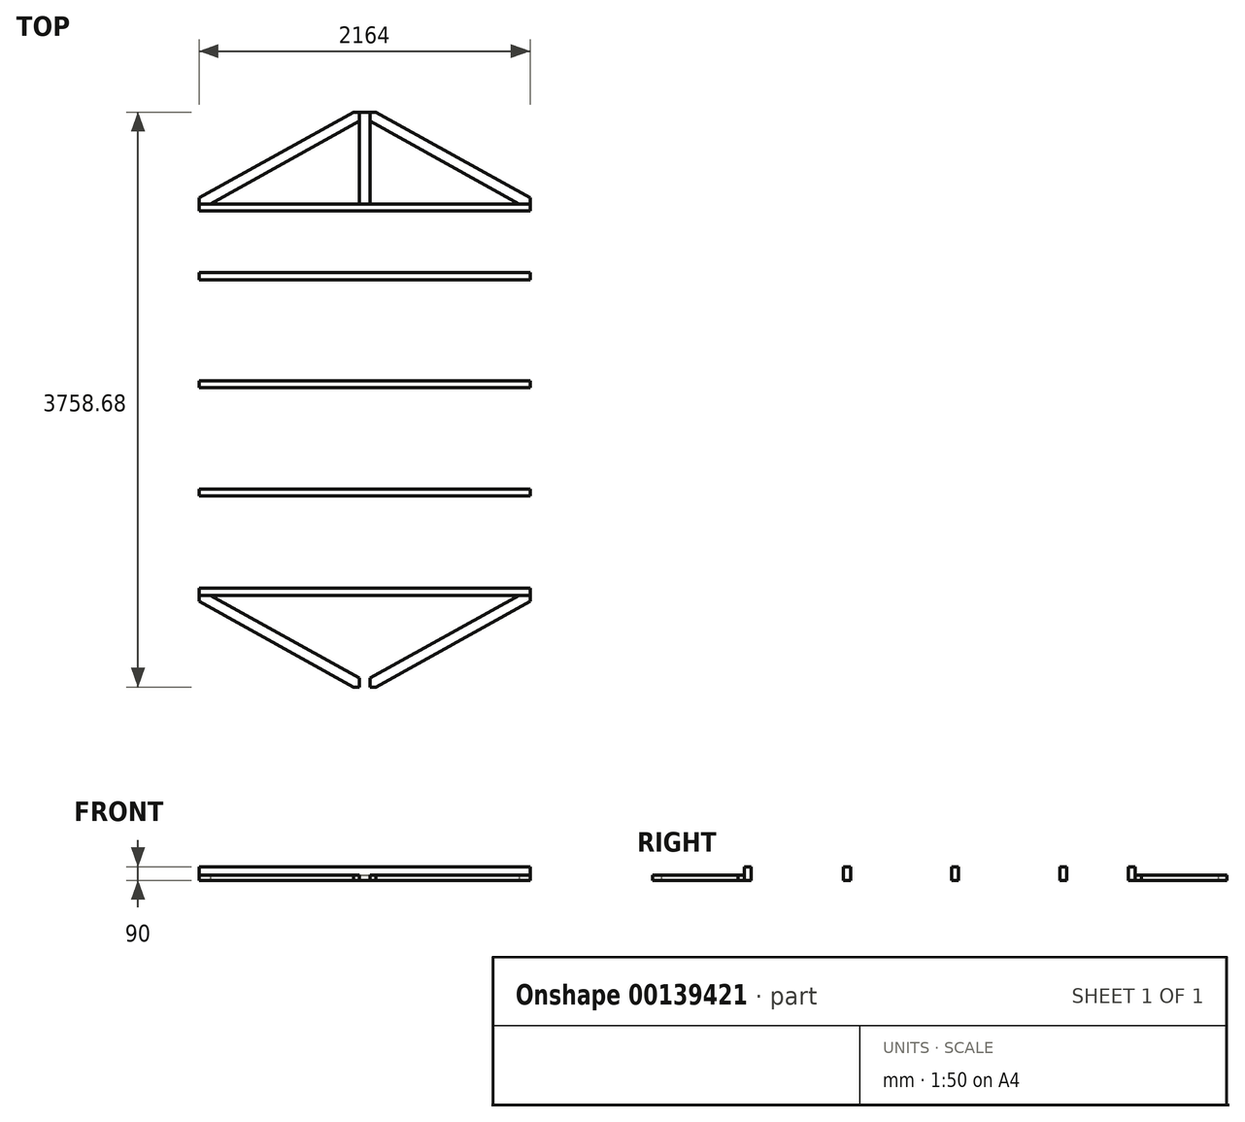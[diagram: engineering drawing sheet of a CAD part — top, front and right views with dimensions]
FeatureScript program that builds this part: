
annotation { "Feature Type Name" : "Feature", "Feature Type Description" : "" }
export const myFeature = defineFeature(function(context is Context, id is Id, definition is map)
    precondition{}
    {
        {
            var Q0;
            Q0=qCreatedBy(makeId("Top.planeOp"),FACE);
            var sketch = newSketch(context, id + "F0", { "sketchPlane" : qUnion([Q0])});
            skLineSegment(sketch, "E0.bottom", {"start": v(1082, 1879.34) * mm, "end": v(-1082, 1879.34) * mm, "construction": true});
            skLineSegment(sketch, "E0.top", {"start": v(1082, -1879.34) * mm, "end": v(-1082, -1879.34) * mm, "construction": true});
            skLineSegment(sketch, "E0.left", {"start": v(1082, 1879.34) * mm, "end": v(1082, -1879.34) * mm, "construction": true});
            skLineSegment(sketch, "E0.right", {"start": v(-1082, 1879.34) * mm, "end": v(-1082, -1879.34) * mm, "construction": true});
            skPoint(sketch, "E0.middle", {"position": v(0, 0) * mm});
            skLineSegment(sketch, "E1.bottom", {"start": v(-1082, -1234.4) * mm, "end": v(1082, -1234.4) * mm});
            skLineSegment(sketch, "E1.top", {"start": v(-1082, -1279.4) * mm, "end": v(1082, -1279.4) * mm});
            skLineSegment(sketch, "E1.left", {"start": v(-1082, -1234.4) * mm, "end": v(-1082, -1279.4) * mm});
            skLineSegment(sketch, "E1.right", {"start": v(1082, -1234.4) * mm, "end": v(1082, -1279.4) * mm});
            skLineSegment(sketch, "E2.bottom", {"start": v(-1082, -584) * mm, "end": v(1082, -584) * mm});
            skLineSegment(sketch, "E2.top", {"start": v(-1082, -629) * mm, "end": v(1082, -629) * mm});
            skLineSegment(sketch, "E2.left", {"start": v(-1082, -584) * mm, "end": v(-1082, -629) * mm});
            skLineSegment(sketch, "E2.right", {"start": v(1082, -584) * mm, "end": v(1082, -629) * mm});
            skLineSegment(sketch, "E3.bottom", {"start": v(-1082, 829.8) * mm, "end": v(1082, 829.8) * mm});
            skLineSegment(sketch, "E3.top", {"start": v(-1082, 784.8) * mm, "end": v(1082, 784.8) * mm});
            skLineSegment(sketch, "E3.left", {"start": v(-1082, 829.8) * mm, "end": v(-1082, 784.8) * mm});
            skLineSegment(sketch, "E3.right", {"start": v(1082, 829.8) * mm, "end": v(1082, 784.8) * mm});
            skLineSegment(sketch, "E4.bottom", {"start": v(-1082, 1279.4) * mm, "end": v(1082, 1279.4) * mm});
            skLineSegment(sketch, "E4.top", {"start": v(-1082, 1234.4) * mm, "end": v(1082, 1234.4) * mm});
            skLineSegment(sketch, "E4.left", {"start": v(-1082, 1279.4) * mm, "end": v(-1082, 1234.4) * mm});
            skLineSegment(sketch, "E4.right", {"start": v(1082, 1279.4) * mm, "end": v(1082, 1234.4) * mm});
            skLineSegment(sketch, "E5.bottom", {"start": v(-1082, 122.9) * mm, "end": v(1082, 122.9) * mm});
            skLineSegment(sketch, "E5.top", {"start": v(-1082, 77.9) * mm, "end": v(1082, 77.9) * mm});
            skLineSegment(sketch, "E5.left", {"start": v(-1082, 122.9) * mm, "end": v(-1082, 77.9) * mm});
            skLineSegment(sketch, "E5.right", {"start": v(1082, 122.9) * mm, "end": v(1082, 77.9) * mm});
            skLineSegment(sketch, "E6", {"start": v(-1082, 1279.4) * mm, "end": v(0, 1879.34) * mm, "construction": true});
            skLineSegment(sketch, "E7", {"start": v(0, 1879.34) * mm, "end": v(1082, 1279.4) * mm, "construction": true});
            skLineSegment(sketch, "E8", {"start": v(-1082, -1279.4) * mm, "end": v(0, -1879.34) * mm, "construction": true});
            skLineSegment(sketch, "E9", {"start": v(0, -1879.34) * mm, "end": v(1082, -1279.4) * mm, "construction": true});
            skLineSegment(sketch, "E10", {"start": v(0, 1879.34) * mm, "end": v(0, -1879.34) * mm, "construction": true});
            skLineSegment(sketch, "E11.bottom", {"start": v(-35, 1879.34) * mm, "end": v(35, 1879.34) * mm});
            skLineSegment(sketch, "E11.top", {"start": v(-35, 1279.4) * mm, "end": v(35, 1279.4) * mm});
            skLineSegment(sketch, "E11.left", {"start": v(-35, 1879.34) * mm, "end": v(-35, 1279.4) * mm});
            skLineSegment(sketch, "E11.right", {"start": v(35, 1879.34) * mm, "end": v(35, 1279.4) * mm});
            skLineSegment(sketch, "E12.bottom", {"start": v(-35, -1279.4) * mm, "end": v(35, -1279.4) * mm});
            skLineSegment(sketch, "E12.top", {"start": v(-35, -1879.34) * mm, "end": v(35, -1879.34) * mm});
            skLineSegment(sketch, "E12.left", {"start": v(-35, -1279.4) * mm, "end": v(-35, -1879.34) * mm});
            skLineSegment(sketch, "E12.right", {"start": v(35, -1279.4) * mm, "end": v(35, -1879.34) * mm});
            skLineSegment(sketch, "E13", {"start": v(-1009.82, -1279.4) * mm, "end": v(-35, -1819.92) * mm});
            skLineSegment(sketch, "E14", {"start": v(-1082, -1279.4) * mm, "end": v(-1082, -1319.42) * mm});
            skLineSegment(sketch, "E15", {"start": v(-1082, -1319.42) * mm, "end": v(-72.18, -1879.34) * mm});
            skLineSegment(sketch, "E16", {"start": v(-72.18, -1879.34) * mm, "end": v(-35, -1879.34) * mm});
            skLineSegment(sketch, "E17", {"start": v(1009.82, -1279.4) * mm, "end": v(35, -1819.92) * mm});
            skLineSegment(sketch, "E18", {"start": v(1082, -1279.4) * mm, "end": v(1082, -1319.42) * mm});
            skLineSegment(sketch, "E19", {"start": v(1082, -1319.42) * mm, "end": v(72.18, -1879.34) * mm});
            skLineSegment(sketch, "E20", {"start": v(72.18, -1879.34) * mm, "end": v(35, -1879.34) * mm});
            skLineSegment(sketch, "E21", {"start": v(-35, 1879.34) * mm, "end": v(-72.18, 1879.34) * mm});
            skLineSegment(sketch, "E22", {"start": v(-72.18, 1879.34) * mm, "end": v(-1082, 1319.42) * mm});
            skLineSegment(sketch, "E23", {"start": v(-1082, 1319.42) * mm, "end": v(-1082, 1279.4) * mm});
            skLineSegment(sketch, "E24", {"start": v(-35, 1819.92) * mm, "end": v(-1009.82, 1279.4) * mm});
            skLineSegment(sketch, "E25", {"start": v(35, 1819.92) * mm, "end": v(1009.82, 1279.4) * mm});
            skLineSegment(sketch, "E26", {"start": v(35, 1879.34) * mm, "end": v(72.18, 1879.34) * mm});
            skLineSegment(sketch, "E27", {"start": v(72.18, 1879.34) * mm, "end": v(1082, 1319.42) * mm});
            skLineSegment(sketch, "E28", {"start": v(1082, 1319.42) * mm, "end": v(1082, 1279.4) * mm});
            skLineSegment(sketch, "E29", {"start": v(-361, 1234.4) * mm, "end": v(-361, -1234.4) * mm, "construction": true});
            skLineSegment(sketch, "E30", {"start": v(361, 1234.4) * mm, "end": v(361, -1234.4) * mm, "construction": true});
            skSolve(sketch);
        }
        {
            var Q0;
            Q0=makeQuery(id+"F0.imprint","IMPRINT",FACE,{"disambiguationData":[TD([[makeQuery(id+"F0.imprint","IMPRINT",EDGE,{"derivedFrom":sQuery(id+"F0.wireOp",EDGE,"E4.bottom")}),-1.0]])]});
            var Q1;
            Q1=makeQuery(id+"F0.imprint","IMPRINT",FACE,{"disambiguationData":[TD([[makeQuery(id+"F0.imprint","IMPRINT",EDGE,{"derivedFrom":sQuery(id+"F0.wireOp",EDGE,"E3.bottom")}),-1.0]])]});
            var Q2;
            Q2=makeQuery(id+"F0.imprint","IMPRINT",FACE,{"disambiguationData":[TD([[makeQuery(id+"F0.imprint","IMPRINT",EDGE,{"derivedFrom":sQuery(id+"F0.wireOp",EDGE,"E5.bottom")}),-1.0]])]});
            var Q3;
            Q3=makeQuery(id+"F0.imprint","IMPRINT",FACE,{"disambiguationData":[TD([[makeQuery(id+"F0.imprint","IMPRINT",EDGE,{"derivedFrom":sQuery(id+"F0.wireOp",EDGE,"E2.bottom")}),-1.0]])]});
            var Q4;
            Q4=makeQuery(id+"F0.imprint","IMPRINT",FACE,{"disambiguationData":[TD([[makeQuery(id+"F0.imprint","IMPRINT",EDGE,{"derivedFrom":sQuery(id+"F0.wireOp",EDGE,"E1.bottom")}),-1.0]])]});
            extrude(context, id + "F1", {"entities" : qUnion([Q0, Q1, Q2, Q3, Q4]), "depth" : 90 * mm});
        }
        {
            var Q0;
            {var subQ0=sQuery(id+"F0.wireOp",EDGE,"E21");Q0=makeQuery(id+"F0.imprint","IMPRINT",FACE,{"disambiguationData":[TD([[makeQuery(id+"F0.imprint","IMPRINT",EDGE,{"derivedFrom":subQ0}),1.0]])]});}
            var Q1;
            {var subQ3=sQuery(id+"F0.wireOp",EDGE,"E25");Q1=makeQuery(id+"F0.imprint","IMPRINT",FACE,{"disambiguationData":[TD([[makeQuery(id+"F0.imprint","IMPRINT",EDGE,{"derivedFrom":subQ3}),1.0]])]});}
            var Q2;
            {var subQ1=sQuery(id+"F0.wireOp",EDGE,"E13");Q2=makeQuery(id+"F0.imprint","IMPRINT",FACE,{"disambiguationData":[TD([[makeQuery(id+"F0.imprint","IMPRINT",EDGE,{"derivedFrom":subQ1}),-1.0]])]});}
            var Q3;
            {var subQ1=sQuery(id+"F0.wireOp",EDGE,"E17");Q3=makeQuery(id+"F0.imprint","IMPRINT",FACE,{"disambiguationData":[TD([[makeQuery(id+"F0.imprint","IMPRINT",EDGE,{"derivedFrom":subQ1}),1.0]])]});}
            extrude(context, id + "F2", {"entities" : qUnion([Q0, Q1, Q2, Q3]), "depth" : 35 * mm});
        }
        {
            var Q0;
            {var subQ4=sQuery(id+"F0.wireOp",EDGE,"E11.bottom");Q0=makeQuery(id+"F0.imprint","IMPRINT",FACE,{"disambiguationData":[TD([[makeQuery(id+"F0.imprint","IMPRINT",EDGE,{"derivedFrom":subQ4}),-1.0]])]});}
            var Q1;
            {var subQ3=sQuery(id+"F0.wireOp",EDGE,"E12.bottom");Q1=makeQuery(id+"F0.imprint","IMPRINT",FACE,{"disambiguationData":[TD([[makeQuery(id+"F0.imprint","IMPRINT",EDGE,{"derivedFrom":subQ3}),-1.0]])]});}
            extrude(context, id + "F3", {"entities" : qUnion([Q0, Q1]), "depth" : 35 * mm});
        }
    });
